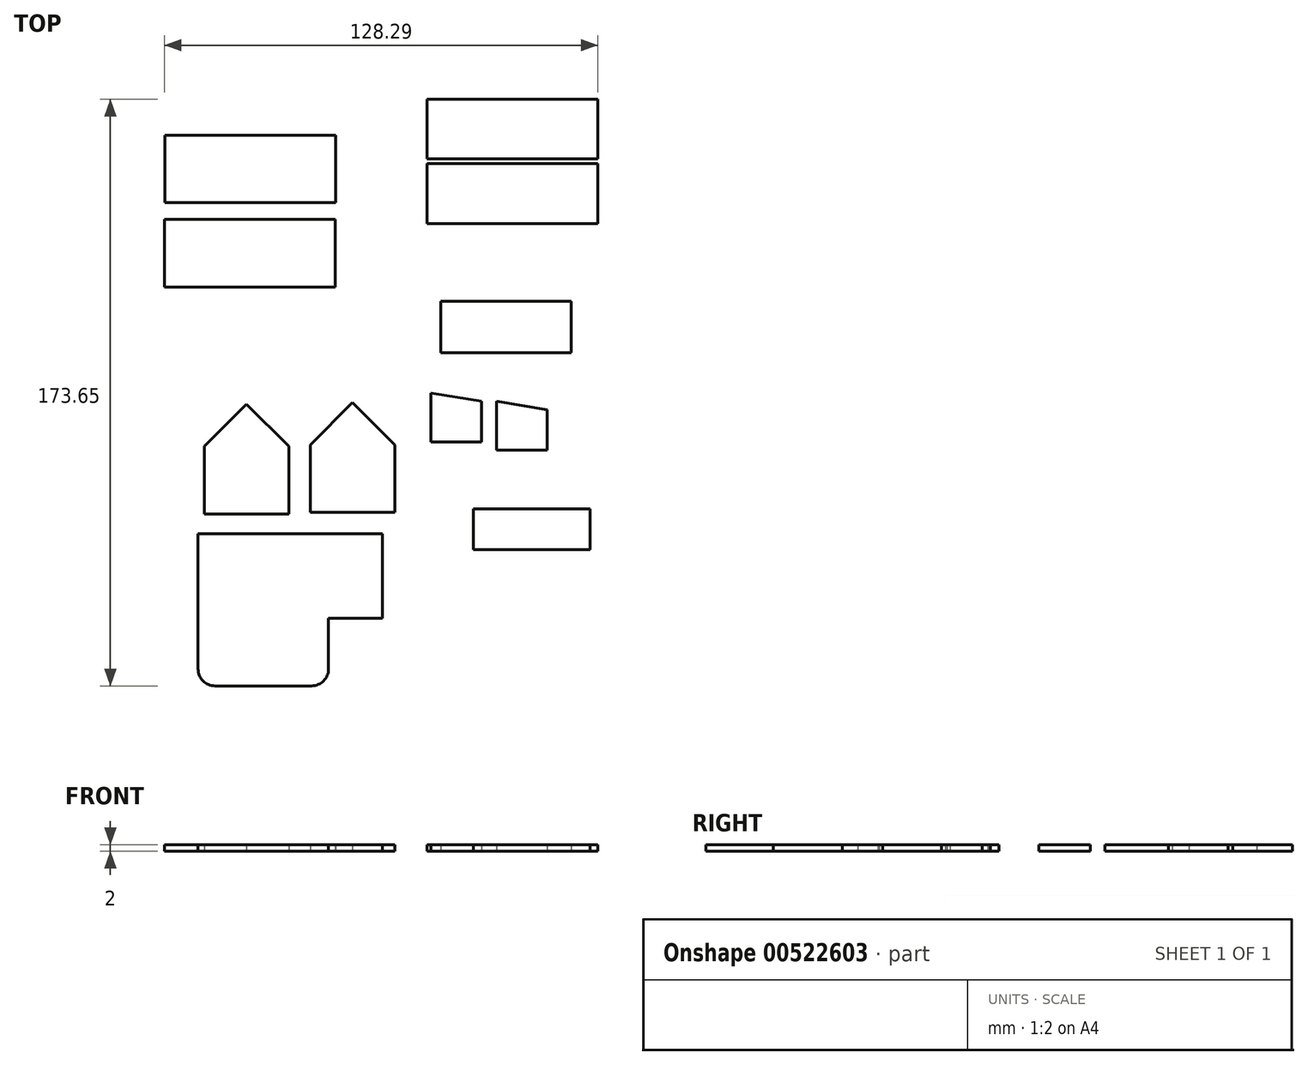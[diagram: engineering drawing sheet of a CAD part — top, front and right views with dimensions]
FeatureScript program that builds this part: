
annotation { "Feature Type Name" : "Feature", "Feature Type Description" : "" }
export const myFeature = defineFeature(function(context is Context, id is Id, definition is map)
    precondition{}
    {
        {
            var Q0;
            Q0=qCreatedBy(makeId("Top.planeOp"),FACE);
            var sketch = newSketch(context, id + "F0", { "sketchPlane" : qUnion([Q0])});
            skLineSegment(sketch, "E0.bottom", {"start": v(-64.4, 62) * mm, "end": v(-13.82, 62) * mm});
            skLineSegment(sketch, "E0.top", {"start": v(-64.4, 42) * mm, "end": v(-13.82, 42) * mm});
            skLineSegment(sketch, "E0.left", {"start": v(-64.4, 62) * mm, "end": v(-64.4, 42) * mm});
            skLineSegment(sketch, "E0.right", {"start": v(-13.82, 62) * mm, "end": v(-13.82, 42) * mm});
            skSolve(sketch);
        }
        {
            var Q0;
            Q0=qCreatedBy(makeId("Top.planeOp"),FACE);
            var sketch = newSketch(context, id + "F1", { "sketchPlane" : qUnion([Q0])});
            skLineSegment(sketch, "E1.bottom", {"start": v(-64.58, 37) * mm, "end": v(-13.99, 37) * mm});
            skLineSegment(sketch, "E1.top", {"start": v(-64.58, 17) * mm, "end": v(-13.99, 17) * mm});
            skLineSegment(sketch, "E1.left", {"start": v(-64.58, 37) * mm, "end": v(-64.58, 17) * mm});
            skLineSegment(sketch, "E1.right", {"start": v(-13.99, 37) * mm, "end": v(-13.99, 17) * mm});
            skSolve(sketch);
        }
        {
            var Q0;
            Q0=qCreatedBy(makeId("Top.planeOp"),FACE);
            var sketch = newSketch(context, id + "F2", { "sketchPlane" : qUnion([Q0])});
            skLineSegment(sketch, "E2.bottom", {"start": v(13.12, 72.59) * mm, "end": v(63.7, 72.59) * mm});
            skLineSegment(sketch, "E2.top", {"start": v(13.12, 54.91) * mm, "end": v(63.7, 54.91) * mm});
            skLineSegment(sketch, "E2.left", {"start": v(13.12, 72.59) * mm, "end": v(13.12, 54.91) * mm});
            skLineSegment(sketch, "E2.right", {"start": v(63.7, 72.59) * mm, "end": v(63.7, 54.91) * mm});
            skSolve(sketch);
        }
        {
            var Q0;
            Q0=qCreatedBy(makeId("Top.planeOp"),FACE);
            var sketch = newSketch(context, id + "F3", { "sketchPlane" : qUnion([Q0])});
            skLineSegment(sketch, "E3.bottom", {"start": v(13.12, 53.53) * mm, "end": v(63.7, 53.53) * mm});
            skLineSegment(sketch, "E3.top", {"start": v(13.12, 35.85) * mm, "end": v(63.7, 35.85) * mm});
            skLineSegment(sketch, "E3.left", {"start": v(13.12, 53.53) * mm, "end": v(13.12, 35.85) * mm});
            skLineSegment(sketch, "E3.right", {"start": v(63.7, 53.53) * mm, "end": v(63.7, 35.85) * mm});
            skSolve(sketch);
        }
        {
            var Q0;
            Q0=qCreatedBy(makeId("Top.planeOp"),FACE);
            var sketch = newSketch(context, id + "F4", { "sketchPlane" : qUnion([Q0])});
            skLineSegment(sketch, "E4.bottom", {"start": v(-52.77, -30.15) * mm, "end": v(-27.77, -30.15) * mm});
            skLineSegment(sketch, "E4.top", {"start": v(-52.77, -50.15) * mm, "end": v(-27.77, -50.15) * mm});
            skLineSegment(sketch, "E4.left", {"start": v(-52.77, -30.15) * mm, "end": v(-52.77, -50.15) * mm});
            skLineSegment(sketch, "E4.right", {"start": v(-27.77, -30.15) * mm, "end": v(-27.77, -50.15) * mm});
            skLineSegment(sketch, "E5", {"start": v(-52.77, -30.15) * mm, "end": v(-40.27, -17.65) * mm});
            skLineSegment(sketch, "E6", {"start": v(-40.27, -17.65) * mm, "end": v(-27.77, -30.15) * mm});
            skSolve(sketch);
        }
        {
            var Q0;
            Q0=qCreatedBy(makeId("Top.planeOp"),FACE);
            var sketch = newSketch(context, id + "F5", { "sketchPlane" : qUnion([Q0])});
            skLineSegment(sketch, "E7.bottom", {"start": v(33.77, -19.28) * mm, "end": v(48.77, -19.28) * mm});
            skLineSegment(sketch, "E7.top", {"start": v(33.77, -31.28) * mm, "end": v(48.77, -31.28) * mm});
            skLineSegment(sketch, "E7.left", {"start": v(33.77, -19.28) * mm, "end": v(33.77, -31.28) * mm});
            skLineSegment(sketch, "E7.right", {"start": v(48.77, -19.28) * mm, "end": v(48.77, -31.28) * mm});
            skLineSegment(sketch, "E8", {"start": v(33.77, -19.28) * mm, "end": v(33.77, -16.78) * mm});
            skLineSegment(sketch, "E9", {"start": v(33.77, -16.78) * mm, "end": v(48.77, -19.28) * mm});
            skSolve(sketch);
        }
        {
            var Q0;
            Q0=qCreatedBy(makeId("Top.planeOp"),FACE);
            var sketch = newSketch(context, id + "F6", { "sketchPlane" : qUnion([Q0])});
            skLineSegment(sketch, "E10.bottom", {"start": v(-21.39, -29.71) * mm, "end": v(3.61, -29.71) * mm});
            skLineSegment(sketch, "E10.top", {"start": v(-21.39, -49.71) * mm, "end": v(3.61, -49.71) * mm});
            skLineSegment(sketch, "E10.left", {"start": v(-21.39, -29.71) * mm, "end": v(-21.39, -49.71) * mm});
            skLineSegment(sketch, "E10.right", {"start": v(3.61, -29.71) * mm, "end": v(3.61, -49.71) * mm});
            skLineSegment(sketch, "E11", {"start": v(-21.39, -29.71) * mm, "end": v(-8.89, -17.21) * mm});
            skLineSegment(sketch, "E12", {"start": v(-8.89, -17.21) * mm, "end": v(3.61, -29.71) * mm});
            skSolve(sketch);
        }
        {
            var Q0;
            Q0=qCreatedBy(makeId("Top.planeOp"),FACE);
            var sketch = newSketch(context, id + "F7", { "sketchPlane" : qUnion([Q0])});
            skLineSegment(sketch, "E13.bottom", {"start": v(-54.6, -56.06) * mm, "end": v(0, -56.06) * mm});
            skLineSegment(sketch, "E13.top", {"start": v(-54.6, -81.06) * mm, "end": v(0, -81.06) * mm});
            skLineSegment(sketch, "E13.left", {"start": v(-54.6, -56.06) * mm, "end": v(-54.6, -81.06) * mm});
            skLineSegment(sketch, "E13.right", {"start": v(0, -56.06) * mm, "end": v(0, -81.06) * mm});
            skLineSegment(sketch, "E14.bottom", {"start": v(-54.6, -81.06) * mm, "end": v(-15.98, -81.06) * mm});
            skLineSegment(sketch, "E14.top", {"start": v(-49.6, -101.06) * mm, "end": v(-20.98, -101.06) * mm});
            skLineSegment(sketch, "E14.left", {"start": v(-54.6, -81.06) * mm, "end": v(-54.6, -96.06) * mm});
            skLineSegment(sketch, "E14.right", {"start": v(-15.98, -81.06) * mm, "end": v(-15.98, -96.06) * mm});
            skPoint(sketch, "E15", {"position": v(-54.6, -94.47) * mm});
            skPoint(sketch, "E16", {"position": v(-47.23, -101.06) * mm});
            skPoint(sketch, "E17", {"position": v(-15.98, -94.47) * mm});
            skPoint(sketch, "E18", {"position": v(-32.52, -101.06) * mm});
            skPoint(sketch, "E19.visualSharp", {"position": v(-54.6, -101.06) * mm});
            skArc(sketch, "E19.filletArc", {"start": v(-54.6, -96.06) * mm, "mid": v(-53.13, -99.6) * mm, "end": v(-49.6, -101.06) * mm});
            skPoint(sketch, "E20.visualSharp", {"position": v(-15.98, -101.06) * mm});
            skArc(sketch, "E20.filletArc", {"start": v(-20.98, -101.06) * mm, "mid": v(-17.44, -99.6) * mm, "end": v(-15.98, -96.06) * mm});
            skSolve(sketch);
        }
        {
            var Q0;
            Q0=qCreatedBy(makeId("Top.planeOp"),FACE);
            var sketch = newSketch(context, id + "F8", { "sketchPlane" : qUnion([Q0])});
            skLineSegment(sketch, "E21.bottom", {"start": v(14.3, -16.81) * mm, "end": v(29.3, -16.81) * mm});
            skLineSegment(sketch, "E21.top", {"start": v(14.3, -28.81) * mm, "end": v(29.3, -28.81) * mm});
            skLineSegment(sketch, "E21.left", {"start": v(14.3, -16.81) * mm, "end": v(14.3, -28.81) * mm});
            skLineSegment(sketch, "E21.right", {"start": v(29.3, -16.81) * mm, "end": v(29.3, -28.81) * mm});
            skLineSegment(sketch, "E22", {"start": v(14.3, -16.81) * mm, "end": v(14.3, -14.31) * mm});
            skLineSegment(sketch, "E23", {"start": v(14.3, -14.31) * mm, "end": v(29.3, -16.81) * mm});
            skSolve(sketch);
        }
        {
            var Q0;
            Q0=qCreatedBy(makeId("Top.planeOp"),FACE);
            var sketch = newSketch(context, id + "F9", { "sketchPlane" : qUnion([Q0])});
            skLineSegment(sketch, "E24.bottom", {"start": v(17.29, 12.76) * mm, "end": v(55.9, 12.76) * mm});
            skLineSegment(sketch, "E24.top", {"start": v(17.29, -2.44) * mm, "end": v(55.9, -2.44) * mm});
            skLineSegment(sketch, "E24.left", {"start": v(17.29, 12.76) * mm, "end": v(17.29, -2.44) * mm});
            skLineSegment(sketch, "E24.right", {"start": v(55.9, 12.76) * mm, "end": v(55.9, -2.44) * mm});
            skSolve(sketch);
        }
        {
            var Q0;
            Q0=qCreatedBy(makeId("Top.planeOp"),FACE);
            var sketch = newSketch(context, id + "F10", { "sketchPlane" : qUnion([Q0])});
            skLineSegment(sketch, "E25.bottom", {"start": v(26.84, -48.69) * mm, "end": v(61.45, -48.69) * mm});
            skLineSegment(sketch, "E25.top", {"start": v(26.84, -60.69) * mm, "end": v(61.45, -60.69) * mm});
            skLineSegment(sketch, "E25.left", {"start": v(26.84, -48.69) * mm, "end": v(26.84, -60.69) * mm});
            skLineSegment(sketch, "E25.right", {"start": v(61.45, -48.69) * mm, "end": v(61.45, -60.69) * mm});
            skSolve(sketch);
        }
        {
            var Q0;
            Q0=makeQuery(id+"F6.imprint","IMPRINT",FACE,{"disambiguationData":[TD([[makeQuery(id+"F6.imprint","IMPRINT",EDGE,{"derivedFrom":sQuery(id+"F6.wireOp",EDGE,"E10.bottom")}),1.0]])]});
            var Q1;
            Q1=makeQuery(id+"F6.imprint","IMPRINT",FACE,{"disambiguationData":[TD([[makeQuery(id+"F6.imprint","IMPRINT",EDGE,{"derivedFrom":sQuery(id+"F6.wireOp",EDGE,"E10.bottom")}),-1.0]])]});
            var Q2;
            Q2=makeQuery(id+"F3.imprint","IMPRINT",FACE,{"disambiguationData":[TD([[makeQuery(id+"F3.imprint","IMPRINT",EDGE,{"derivedFrom":sQuery(id+"F3.wireOp",EDGE,"E3.bottom")}),-1.0]])]});
            var Q3;
            Q3=makeQuery(id+"F4.imprint","IMPRINT",FACE,{"disambiguationData":[TD([[makeQuery(id+"F4.imprint","IMPRINT",EDGE,{"derivedFrom":sQuery(id+"F4.wireOp",EDGE,"E4.bottom")}),1.0]])]});
            var Q4;
            Q4=makeQuery(id+"F0.imprint","IMPRINT",FACE,{"disambiguationData":[TD([[makeQuery(id+"F0.imprint","IMPRINT",EDGE,{"derivedFrom":sQuery(id+"F0.wireOp",EDGE,"E0.bottom")}),-1.0]])]});
            var Q5;
            Q5=makeQuery(id+"F10.imprint","IMPRINT",FACE,{"disambiguationData":[TD([[makeQuery(id+"F10.imprint","IMPRINT",EDGE,{"derivedFrom":sQuery(id+"F10.wireOp",EDGE,"E25.bottom")}),-1.0]])]});
            var Q6;
            Q6=makeQuery(id+"F5.imprint","IMPRINT",FACE,{"disambiguationData":[TD([[makeQuery(id+"F5.imprint","IMPRINT",EDGE,{"derivedFrom":sQuery(id+"F5.wireOp",EDGE,"E7.bottom")}),1.0]])]});
            var Q7;
            Q7=makeQuery(id+"F4.imprint","IMPRINT",FACE,{"disambiguationData":[TD([[makeQuery(id+"F4.imprint","IMPRINT",EDGE,{"derivedFrom":sQuery(id+"F4.wireOp",EDGE,"E4.bottom")}),-1.0]])]});
            var Q8;
            Q8=makeQuery(id+"F5.imprint","IMPRINT",FACE,{"disambiguationData":[TD([[makeQuery(id+"F5.imprint","IMPRINT",EDGE,{"derivedFrom":sQuery(id+"F5.wireOp",EDGE,"E7.bottom")}),-1.0]])]});
            var Q9;
            Q9=makeQuery(id+"F1.imprint","IMPRINT",FACE,{"disambiguationData":[TD([[makeQuery(id+"F1.imprint","IMPRINT",EDGE,{"derivedFrom":sQuery(id+"F1.wireOp",EDGE,"E1.bottom")}),-1.0]])]});
            var Q10;
            Q10=makeQuery(id+"F8.imprint","IMPRINT",FACE,{"disambiguationData":[TD([[makeQuery(id+"F8.imprint","IMPRINT",EDGE,{"derivedFrom":sQuery(id+"F8.wireOp",EDGE,"E21.bottom")}),-1.0]])]});
            var Q11;
            Q11=makeQuery(id+"F9.imprint","IMPRINT",FACE,{"disambiguationData":[TD([[makeQuery(id+"F9.imprint","IMPRINT",EDGE,{"derivedFrom":sQuery(id+"F9.wireOp",EDGE,"E24.bottom")}),-1.0]])]});
            var Q12;
            Q12=makeQuery(id+"F8.imprint","IMPRINT",FACE,{"disambiguationData":[TD([[makeQuery(id+"F8.imprint","IMPRINT",EDGE,{"derivedFrom":sQuery(id+"F8.wireOp",EDGE,"E21.bottom")}),1.0]])]});
            var Q13;
            Q13=makeQuery(id+"F2.imprint","IMPRINT",FACE,{"disambiguationData":[TD([[makeQuery(id+"F2.imprint","IMPRINT",EDGE,{"derivedFrom":sQuery(id+"F2.wireOp",EDGE,"E2.bottom")}),-1.0]])]});
            var Q14;
            Q14=makeQuery(id+"F7.imprint","IMPRINT",FACE,{"disambiguationData":[TD([[makeQuery(id+"F7.imprint","IMPRINT",EDGE,{"derivedFrom":sQuery(id+"F7.wireOp",EDGE,"E13.bottom")}),-1.0]])]});
            var Q15;
            Q15=makeQuery(id+"F7.imprint","IMPRINT",FACE,{"disambiguationData":[TD([[makeQuery(id+"F7.imprint","IMPRINT",EDGE,{"derivedFrom":sQuery(id+"F7.wireOp",EDGE,"E14.top")}),1.0]])]});
            extrude(context, id + "F11", {"entities" : qUnion([Q0, Q1, Q2, Q3, Q4, Q5, Q6, Q7, Q8, Q9, Q10, Q11, Q12, Q13, Q14, Q15]), "depth" : 2 * mm, "offsetDistance" : 25 * mm});
        }
    });
